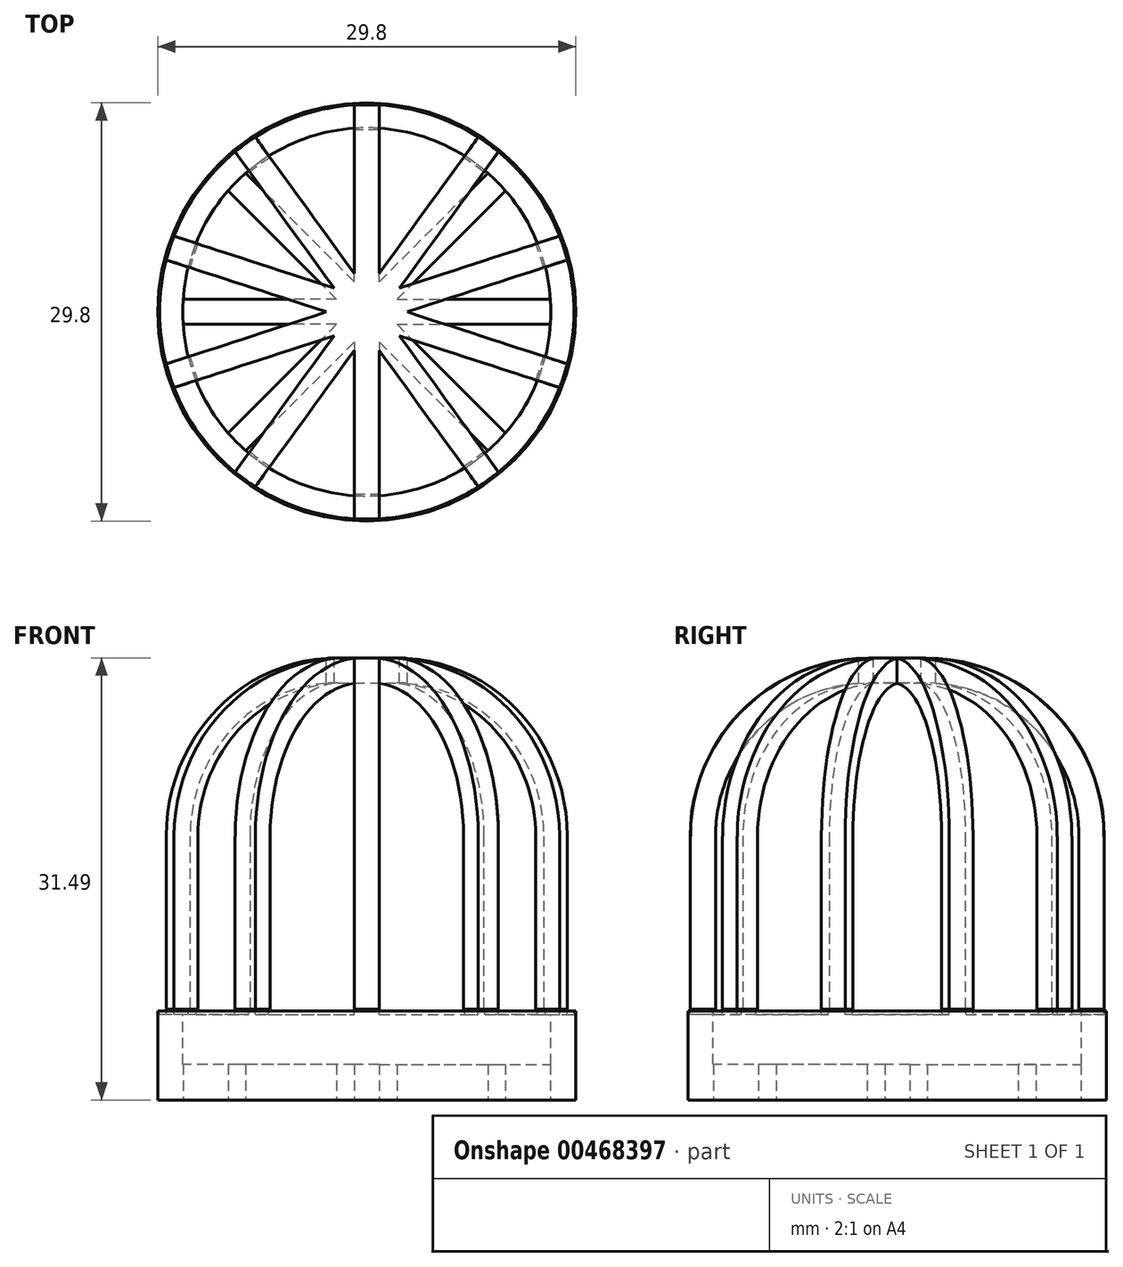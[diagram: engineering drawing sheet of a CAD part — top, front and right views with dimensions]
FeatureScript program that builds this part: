
annotation { "Feature Type Name" : "Feature", "Feature Type Description" : "" }
export const myFeature = defineFeature(function(context is Context, id is Id, definition is map)
    precondition{}
    {
        {
            var Q0;
            Q0=qCreatedBy(makeId("Top.planeOp"),FACE);
            var sketch = newSketch(context, id + "F0", { "sketchPlane" : qUnion([Q0])});
            skCircle(sketch, "E0", {"center": v(0, 0) * mm, "radius": 14.9 * mm});
            skSolve(sketch);
        }
        {
            var Q0;
            Q0 = qSketchRegion(id + "F0", true);
            extrude(context, id + "F1", {"entities" : qUnion([Q0]), "depth" : 6.35 * mm});
        }
        {
            var Q0;
            Q0=makeQuery(id+"F1.opExtrude","CAP_FACE",FACE,{"disambiguationData":[OSD([sQuery(id+"F0.wireOp",EDGE,"E0")])],"isStart":false});
            var sketch = newSketch(context, id + "F2", { "sketchPlane" : qUnion([Q0])});
            skCircle(sketch, "E1", {"center": v(0, 0) * mm, "radius": 13.12 * mm});
            skSolve(sketch);
        }
        {
            var Q0;
            Q0=makeQuery(id+"F2.imprint","IMPRINT",FACE,{"disambiguationData":[TD([[makeQuery(id+"F2.imprint","IMPRINT",EDGE,{"derivedFrom":sQuery(id+"F2.wireOp",EDGE,"E1")}),1.0]])]});
            extrude(context, id + "F3", {"entities" : qUnion([Q0]), "operationType" : NewBodyOperationType.REMOVE, "oppositeDirection" : true, "depth" : 25.4 * mm});
        }
        {
            var Q0;
            Q0=qCreatedBy(makeId("Front.planeOp"),FACE);
            var sketch = newSketch(context, id + "F4", { "sketchPlane" : qUnion([Q0])});
            skLineSegment(sketch, "E2", {"start": v(0, 6.47) * mm, "end": v(0, 31.49) * mm});
            skLineSegment(sketch, "E3", {"start": v(0, 31.49) * mm, "end": v(2.06, 31.49) * mm});
            skLineSegment(sketch, "E4", {"start": v(0, 6.47) * mm, "end": v(14.76, 6.47) * mm});
            skLineSegment(sketch, "E5", {"start": v(14.76, 6.47) * mm, "end": v(14.76, 18.79) * mm});
            skPoint(sketch, "E6.orphan", {"position": v(15.8, 31.49) * mm});
            skPoint(sketch, "E7.visualSharp", {"position": v(14.76, 31.49) * mm});
            skArc(sketch, "E7.filletArc", {"start": v(14.76, 18.79) * mm, "mid": v(11.04, 27.77) * mm, "end": v(2.06, 31.49) * mm});
            skSolve(sketch);
        }
        {
            var Q0;
            Q0 = qSketchRegion(id + "F4", true);
            var Q1;
            Q1=sQuery(id+"F4.wireOp",EDGE,"E2");
            revolve(context, id + "F5", {"operationType" : NewBodyOperationType.ADD, "entities" : qUnion([Q0]), "axis" : qUnion([Q1]), "revolveType" : RevolveType.FULL});
        }
        {
            var Q0;
            Q0=makeQuery(id+"F5.opRevolve","SWEPT_FACE",FACE,{"disambiguationData":[OSD([sQuery(id+"F4.wireOp",EDGE,"E4")])]});
            shell(context, id + "F6", {"entities" : qUnion([Q0]), "thickness" : 1.78 * mm});
        }
        {
            var Q0;
            Q0=makeQuery(id+"F5.opRevolve","SWEPT_FACE",FACE,{"disambiguationData":[OSD([sQuery(id+"F4.wireOp",EDGE,"E3")])]});
            var sketch = newSketch(context, id + "F7", { "sketchPlane" : qUnion([Q0])});
            skLineSegment(sketch, "E8", {"start": v(0, 0) * mm, "end": v(0, 14.8) * mm});
            skLineSegment(sketch, "E9", {"start": v(-0.89, 1.86) * mm, "end": v(-0.89, 14.74) * mm});
            skLineSegment(sketch, "E10", {"start": v(0.89, 1.86) * mm, "end": v(0.89, 14.74) * mm});
            skCircle(sketch, "E11", {"center": v(0, 0) * mm, "radius": 14.76 * mm});
            skLineSegment(sketch, "E12.1.0", {"start": v(-0.37, 2.02) * mm, "end": v(-7.94, 12.45) * mm});
            skLineSegment(sketch, "E12.1.1", {"start": v(-1.81, 0.98) * mm, "end": v(-9.38, 11.4) * mm});
            skLineSegment(sketch, "E12.2.0", {"start": v(-1.5, 1.42) * mm, "end": v(-13.74, 5.4) * mm});
            skLineSegment(sketch, "E12.2.1", {"start": v(-2.04, -0.27) * mm, "end": v(-14.3, 3.7) * mm});
            skLineSegment(sketch, "E12.3.0", {"start": v(-2.04, 0.27) * mm, "end": v(-14.3, -3.7) * mm});
            skLineSegment(sketch, "E12.3.1", {"start": v(-1.5, -1.42) * mm, "end": v(-13.74, -5.4) * mm});
            skLineSegment(sketch, "E12.4.0", {"start": v(-1.81, -0.98) * mm, "end": v(-9.38, -11.4) * mm});
            skLineSegment(sketch, "E12.4.1", {"start": v(-0.37, -2.02) * mm, "end": v(-7.94, -12.45) * mm});
            skLineSegment(sketch, "E12.5.0", {"start": v(-0.89, -1.86) * mm, "end": v(-0.89, -14.74) * mm});
            skLineSegment(sketch, "E12.5.1", {"start": v(0.89, -1.86) * mm, "end": v(0.89, -14.74) * mm});
            skLineSegment(sketch, "E12.6.0", {"start": v(0.37, -2.02) * mm, "end": v(7.94, -12.45) * mm});
            skLineSegment(sketch, "E12.6.1", {"start": v(1.81, -0.98) * mm, "end": v(9.38, -11.4) * mm});
            skLineSegment(sketch, "E12.7.0", {"start": v(1.5, -1.42) * mm, "end": v(13.74, -5.4) * mm});
            skLineSegment(sketch, "E12.7.1", {"start": v(2.04, 0.27) * mm, "end": v(14.3, -3.7) * mm});
            skLineSegment(sketch, "E12.8.0", {"start": v(2.04, -0.27) * mm, "end": v(14.3, 3.7) * mm});
            skLineSegment(sketch, "E12.8.1", {"start": v(1.5, 1.42) * mm, "end": v(13.74, 5.4) * mm});
            skLineSegment(sketch, "E12.9.0", {"start": v(1.81, 0.98) * mm, "end": v(9.38, 11.4) * mm});
            skLineSegment(sketch, "E12.9.1", {"start": v(0.37, 2.02) * mm, "end": v(7.94, 12.45) * mm});
            skSolve(sketch);
        }
        {
            var Q0;
            {var subQ0=sQuery(id+"F7.wireOp",EDGE,"E12.4.1");var subQ1=sQuery(id+"F7.wireOp",EDGE,"E11");var subQ2=makeQuery(id+"F7.imprint","INTERSECT",VERTEX,{"derivedFrom":[subQ1,subQ0]});Q0=makeQuery(id+"F7.imprint","IMPRINT",FACE,{"disambiguationData":[TD([[makeQuery(id+"F7.imprint","IMPRINT",EDGE,{"disambiguationData":[TD([[subQ2,-1.0]])],"derivedFrom":subQ1}),1.0]])]});}
            var Q1;
            {var subQ0=sQuery(id+"F7.wireOp",EDGE,"E12.3.1");var subQ1=sQuery(id+"F7.wireOp",EDGE,"E11");var subQ2=makeQuery(id+"F7.imprint","INTERSECT",VERTEX,{"derivedFrom":[subQ1,subQ0]});Q1=makeQuery(id+"F7.imprint","IMPRINT",FACE,{"disambiguationData":[TD([[makeQuery(id+"F7.imprint","IMPRINT",EDGE,{"disambiguationData":[TD([[subQ2,-1.0]])],"derivedFrom":subQ1}),1.0]])]});}
            var Q2;
            {var subQ0=sQuery(id+"F7.wireOp",EDGE,"E12.2.1");var subQ1=sQuery(id+"F7.wireOp",EDGE,"E11");var subQ2=makeQuery(id+"F7.imprint","INTERSECT",VERTEX,{"derivedFrom":[subQ1,subQ0]});Q2=makeQuery(id+"F7.imprint","IMPRINT",FACE,{"disambiguationData":[TD([[makeQuery(id+"F7.imprint","IMPRINT",EDGE,{"disambiguationData":[TD([[subQ2,-1.0]])],"derivedFrom":subQ1}),1.0]])]});}
            var Q3;
            {var subQ0=sQuery(id+"F7.wireOp",EDGE,"E12.5.1");var subQ1=sQuery(id+"F7.wireOp",EDGE,"E11");var subQ2=makeQuery(id+"F7.imprint","INTERSECT",VERTEX,{"derivedFrom":[subQ1,subQ0]});Q3=makeQuery(id+"F7.imprint","IMPRINT",FACE,{"disambiguationData":[TD([[makeQuery(id+"F7.imprint","IMPRINT",EDGE,{"disambiguationData":[TD([[subQ2,-1.0]])],"derivedFrom":subQ1}),1.0]])]});}
            var Q4;
            {var subQ0=sQuery(id+"F7.wireOp",EDGE,"E12.6.1");var subQ1=sQuery(id+"F7.wireOp",EDGE,"E11");var subQ2=makeQuery(id+"F7.imprint","INTERSECT",VERTEX,{"derivedFrom":[subQ1,subQ0]});Q4=makeQuery(id+"F7.imprint","IMPRINT",FACE,{"disambiguationData":[TD([[makeQuery(id+"F7.imprint","IMPRINT",EDGE,{"disambiguationData":[TD([[subQ2,-1.0]])],"derivedFrom":subQ1}),1.0]])]});}
            var Q5;
            {var subQ0=sQuery(id+"F7.wireOp",EDGE,"E12.7.1");var subQ1=sQuery(id+"F7.wireOp",EDGE,"E11");var subQ2=makeQuery(id+"F7.imprint","INTERSECT",VERTEX,{"derivedFrom":[subQ1,subQ0]});Q5=makeQuery(id+"F7.imprint","IMPRINT",FACE,{"disambiguationData":[TD([[makeQuery(id+"F7.imprint","IMPRINT",EDGE,{"disambiguationData":[TD([[subQ2,-1.0]])],"derivedFrom":subQ1}),1.0]])]});}
            var Q6;
            {var subQ0=sQuery(id+"F7.wireOp",EDGE,"E12.8.1");var subQ1=sQuery(id+"F7.wireOp",EDGE,"E11");var subQ2=makeQuery(id+"F7.imprint","INTERSECT",VERTEX,{"derivedFrom":[subQ1,subQ0]});Q6=makeQuery(id+"F7.imprint","IMPRINT",FACE,{"disambiguationData":[TD([[makeQuery(id+"F7.imprint","IMPRINT",EDGE,{"disambiguationData":[TD([[subQ2,-1.0]])],"derivedFrom":subQ1}),1.0]])]});}
            var Q7;
            {var subQ0=sQuery(id+"F7.wireOp",EDGE,"E11");var subQ1=sQuery(id+"F7.wireOp",EDGE,"E10");var subQ2=makeQuery(id+"F7.imprint","INTERSECT",VERTEX,{"derivedFrom":[subQ1,subQ0]});Q7=makeQuery(id+"F7.imprint","IMPRINT",FACE,{"disambiguationData":[TD([[makeQuery(id+"F7.imprint","IMPRINT",EDGE,{"disambiguationData":[TD([[subQ2,1.0]])],"derivedFrom":subQ1}),-1.0]])]});}
            var Q8;
            {var subQ0=sQuery(id+"F7.wireOp",EDGE,"E11");var subQ1=sQuery(id+"F7.wireOp",EDGE,"E9");var subQ2=makeQuery(id+"F7.imprint","INTERSECT",VERTEX,{"derivedFrom":[subQ1,subQ0]});Q8=makeQuery(id+"F7.imprint","IMPRINT",FACE,{"disambiguationData":[TD([[makeQuery(id+"F7.imprint","IMPRINT",EDGE,{"disambiguationData":[TD([[subQ2,1.0]])],"derivedFrom":subQ1}),1.0]])]});}
            var Q9;
            {var subQ0=sQuery(id+"F7.wireOp",EDGE,"E12.1.1");var subQ1=sQuery(id+"F7.wireOp",EDGE,"E11");var subQ2=makeQuery(id+"F7.imprint","INTERSECT",VERTEX,{"derivedFrom":[subQ1,subQ0]});Q9=makeQuery(id+"F7.imprint","IMPRINT",FACE,{"disambiguationData":[TD([[makeQuery(id+"F7.imprint","IMPRINT",EDGE,{"disambiguationData":[TD([[subQ2,-1.0]])],"derivedFrom":subQ1}),1.0]])]});}
            extrude(context, id + "F8", {"entities" : qUnion([Q0, Q1, Q2, Q3, Q4, Q5, Q6, Q7, Q8, Q9]), "operationType" : NewBodyOperationType.REMOVE, "oppositeDirection" : true, "depth" : 25.4 * mm});
        }
        {
            var Q0;
            Q0=makeQuery(id+"F1.opExtrude","CAP_FACE",FACE,{"disambiguationData":[OSD([sQuery(id+"F0.wireOp",EDGE,"E0")])],"isStart":true});
            var sketch = newSketch(context, id + "F9", { "sketchPlane" : qUnion([Q0])});
            skCircle(sketch, "E13", {"center": v(0, 0) * mm, "radius": 13.3 * mm});
            skLineSegment(sketch, "E14", {"start": v(0, 0) * mm, "end": v(0, 13.3) * mm});
            skLineSegment(sketch, "E15", {"start": v(0.89, 0) * mm, "end": v(0.89, 13.27) * mm});
            skLineSegment(sketch, "E16", {"start": v(-0.89, 0) * mm, "end": v(-0.89, 13.27) * mm});
            skLineSegment(sketch, "E17.1.0", {"start": v(-0.63, -0.63) * mm, "end": v(-10.01, 8.75) * mm});
            skLineSegment(sketch, "E17.1.1", {"start": v(0.63, 0.63) * mm, "end": v(-8.75, 10.01) * mm});
            skLineSegment(sketch, "E17.2.0", {"start": v(0, -0.89) * mm, "end": v(-13.27, -0.89) * mm});
            skLineSegment(sketch, "E17.2.1", {"start": v(0, 0.89) * mm, "end": v(-13.27, 0.89) * mm});
            skLineSegment(sketch, "E17.3.0", {"start": v(0.63, -0.63) * mm, "end": v(-8.75, -10.01) * mm});
            skLineSegment(sketch, "E17.3.1", {"start": v(-0.63, 0.63) * mm, "end": v(-10.01, -8.75) * mm});
            skLineSegment(sketch, "E17.4.0", {"start": v(0.89, 0) * mm, "end": v(0.89, -13.27) * mm});
            skLineSegment(sketch, "E17.4.1", {"start": v(-0.89, 0) * mm, "end": v(-0.89, -13.27) * mm});
            skLineSegment(sketch, "E17.5.0", {"start": v(0.63, 0.63) * mm, "end": v(10.01, -8.75) * mm});
            skLineSegment(sketch, "E17.5.1", {"start": v(-0.63, -0.63) * mm, "end": v(8.75, -10.01) * mm});
            skLineSegment(sketch, "E17.6.0", {"start": v(0, 0.89) * mm, "end": v(13.27, 0.89) * mm});
            skLineSegment(sketch, "E17.6.1", {"start": v(0, -0.89) * mm, "end": v(13.27, -0.89) * mm});
            skLineSegment(sketch, "E17.7.0", {"start": v(-0.63, 0.63) * mm, "end": v(8.75, 10.01) * mm});
            skLineSegment(sketch, "E17.7.1", {"start": v(0.63, -0.63) * mm, "end": v(10.01, 8.75) * mm});
            skSolve(sketch);
        }
        {
            var Q0;
            {var subQ0=sQuery(id+"F9.wireOp",EDGE,"E17.7.0");var subQ5=sQuery(id+"F9.wireOp",EDGE,"E15");var subQ6=makeQuery(id+"F9.imprint","INTERSECT",VERTEX,{"derivedFrom":[subQ5,subQ0]});Q0=makeQuery(id+"F9.imprint","IMPRINT",FACE,{"disambiguationData":[TD([[makeQuery(id+"F9.imprint","IMPRINT",EDGE,{"disambiguationData":[TD([[subQ6,-1.0]])],"derivedFrom":subQ5}),1.0]])]});}
            var Q1;
            {var subQ0=sQuery(id+"F9.wireOp",EDGE,"E17.1.1");var subQ5=sQuery(id+"F9.wireOp",EDGE,"E16");var subQ6=makeQuery(id+"F9.imprint","INTERSECT",VERTEX,{"derivedFrom":[subQ5,subQ0]});Q1=makeQuery(id+"F9.imprint","IMPRINT",FACE,{"disambiguationData":[TD([[makeQuery(id+"F9.imprint","IMPRINT",EDGE,{"disambiguationData":[TD([[subQ6,-1.0]])],"derivedFrom":subQ5}),-1.0]])]});}
            var Q2;
            {var subQ1=sQuery(id+"F9.wireOp",EDGE,"E17.6.0");var subQ6=sQuery(id+"F9.wireOp",EDGE,"E15");var subQ9=makeQuery(id+"F9.imprint","INTERSECT",VERTEX,{"derivedFrom":[subQ6,subQ1]});Q2=makeQuery(id+"F9.imprint","IMPRINT",FACE,{"disambiguationData":[TD([[makeQuery(id+"F9.imprint","IMPRINT",EDGE,{"disambiguationData":[TD([[subQ9,-1.0]])],"derivedFrom":subQ6}),-1.0]])]});}
            var Q3;
            {var subQ1=sQuery(id+"F9.wireOp",EDGE,"E17.1.0");var subQ5=sQuery(id+"F9.wireOp",EDGE,"E17.3.1");var subQ9=makeQuery(id+"F9.imprint","INTERSECT",VERTEX,{"derivedFrom":[subQ1,subQ5]});Q3=makeQuery(id+"F9.imprint","IMPRINT",FACE,{"disambiguationData":[TD([[makeQuery(id+"F9.imprint","IMPRINT",EDGE,{"disambiguationData":[TD([[subQ9,-1.0]])],"derivedFrom":subQ1}),1.0]])]});}
            var Q4;
            {var subQ1=sQuery(id+"F9.wireOp",EDGE,"E17.2.0");var subQ5=sQuery(id+"F9.wireOp",EDGE,"E17.4.1");var subQ9=makeQuery(id+"F9.imprint","INTERSECT",VERTEX,{"derivedFrom":[subQ1,subQ5]});Q4=makeQuery(id+"F9.imprint","IMPRINT",FACE,{"disambiguationData":[TD([[makeQuery(id+"F9.imprint","IMPRINT",EDGE,{"disambiguationData":[TD([[subQ9,-1.0]])],"derivedFrom":subQ1}),1.0]])]});}
            var Q5;
            {var subQ1=sQuery(id+"F9.wireOp",EDGE,"E16");var subQ5=sQuery(id+"F9.wireOp",EDGE,"E17.2.1");var subQ6=makeQuery(id+"F9.imprint","INTERSECT",VERTEX,{"derivedFrom":[subQ1,subQ5]});Q5=makeQuery(id+"F9.imprint","IMPRINT",FACE,{"disambiguationData":[TD([[makeQuery(id+"F9.imprint","IMPRINT",EDGE,{"disambiguationData":[TD([[subQ6,-1.0]])],"derivedFrom":subQ1}),1.0]])]});}
            var Q6;
            {var subQ1=sQuery(id+"F9.wireOp",EDGE,"E17.5.0");var subQ5=sQuery(id+"F9.wireOp",EDGE,"E17.7.1");var subQ9=makeQuery(id+"F9.imprint","INTERSECT",VERTEX,{"derivedFrom":[subQ1,subQ5]});Q6=makeQuery(id+"F9.imprint","IMPRINT",FACE,{"disambiguationData":[TD([[makeQuery(id+"F9.imprint","IMPRINT",EDGE,{"disambiguationData":[TD([[subQ9,-1.0]])],"derivedFrom":subQ1}),1.0]])]});}
            var Q7;
            {var subQ1=sQuery(id+"F9.wireOp",EDGE,"E17.4.0");var subQ5=sQuery(id+"F9.wireOp",EDGE,"E17.6.1");var subQ9=makeQuery(id+"F9.imprint","INTERSECT",VERTEX,{"derivedFrom":[subQ1,subQ5]});Q7=makeQuery(id+"F9.imprint","IMPRINT",FACE,{"disambiguationData":[TD([[makeQuery(id+"F9.imprint","IMPRINT",EDGE,{"disambiguationData":[TD([[subQ9,-1.0]])],"derivedFrom":subQ1}),1.0]])]});}
            var Q8;
            {var subQ1=sQuery(id+"F9.wireOp",EDGE,"E17.3.0");var subQ5=sQuery(id+"F9.wireOp",EDGE,"E17.5.1");var subQ9=makeQuery(id+"F9.imprint","INTERSECT",VERTEX,{"derivedFrom":[subQ1,subQ5]});Q8=makeQuery(id+"F9.imprint","IMPRINT",FACE,{"disambiguationData":[TD([[makeQuery(id+"F9.imprint","IMPRINT",EDGE,{"disambiguationData":[TD([[subQ9,-1.0]])],"derivedFrom":subQ1}),1.0]])]});}
            var Q9;
            {var subQ5=sQuery(id+"F9.wireOp",EDGE,"E17.4.0");var subQ6=sQuery(id+"F9.wireOp",EDGE,"E15");var subQ7=makeQuery(id+"F9.imprint","INTERSECT",VERTEX,{"derivedFrom":[subQ6,subQ5]});Q9=makeQuery(id+"F9.imprint","IMPRINT",FACE,{"disambiguationData":[TD([[makeQuery(id+"F9.imprint","IMPRINT",EDGE,{"disambiguationData":[TD([[subQ7,-1.0]])],"derivedFrom":subQ6}),1.0]])]});}
            var Q10;
            {var subQ0=sQuery(id+"F9.wireOp",EDGE,"E17.3.1");var subQ1=sQuery(id+"F9.wireOp",EDGE,"E16");var subQ2=makeQuery(id+"F9.imprint","INTERSECT",VERTEX,{"derivedFrom":[subQ1,subQ0]});Q10=makeQuery(id+"F9.imprint","IMPRINT",FACE,{"disambiguationData":[TD([[makeQuery(id+"F9.imprint","IMPRINT",EDGE,{"disambiguationData":[TD([[subQ2,-1.0]])],"derivedFrom":subQ1}),-1.0]])]});}
            var Q11;
            {var subQ0=sQuery(id+"F9.wireOp",EDGE,"E17.5.0");var subQ1=sQuery(id+"F9.wireOp",EDGE,"E15");var subQ2=makeQuery(id+"F9.imprint","INTERSECT",VERTEX,{"derivedFrom":[subQ1,subQ0]});Q11=makeQuery(id+"F9.imprint","IMPRINT",FACE,{"disambiguationData":[TD([[makeQuery(id+"F9.imprint","IMPRINT",EDGE,{"disambiguationData":[TD([[subQ2,-1.0]])],"derivedFrom":subQ1}),1.0]])]});}
            var Q12;
            {var subQ0=sQuery(id+"F9.wireOp",EDGE,"E17.4.0");var subQ1=sQuery(id+"F9.wireOp",EDGE,"E15");var subQ2=makeQuery(id+"F9.imprint","INTERSECT",VERTEX,{"derivedFrom":[subQ1,subQ0]});Q12=makeQuery(id+"F9.imprint","IMPRINT",FACE,{"disambiguationData":[TD([[makeQuery(id+"F9.imprint","IMPRINT",EDGE,{"disambiguationData":[TD([[subQ2,-1.0]])],"derivedFrom":subQ1}),-1.0]])]});}
            var Q13;
            {var subQ0=sQuery(id+"F9.wireOp",EDGE,"E17.6.1");var subQ1=sQuery(id+"F9.wireOp",EDGE,"E17.2.0");var subQ2=makeQuery(id+"F9.imprint","INTERSECT",VERTEX,{"derivedFrom":[subQ1,subQ0]});Q13=makeQuery(id+"F9.imprint","IMPRINT",FACE,{"disambiguationData":[TD([[makeQuery(id+"F9.imprint","IMPRINT",EDGE,{"disambiguationData":[TD([[subQ2,-1.0]])],"derivedFrom":subQ1}),1.0]])]});}
            var Q14;
            {var subQ0=sQuery(id+"F9.wireOp",EDGE,"E17.7.1");var subQ1=sQuery(id+"F9.wireOp",EDGE,"E17.3.0");var subQ2=makeQuery(id+"F9.imprint","INTERSECT",VERTEX,{"derivedFrom":[subQ1,subQ0]});Q14=makeQuery(id+"F9.imprint","IMPRINT",FACE,{"disambiguationData":[TD([[makeQuery(id+"F9.imprint","IMPRINT",EDGE,{"disambiguationData":[TD([[subQ2,-1.0]])],"derivedFrom":subQ1}),1.0]])]});}
            var Q15;
            {var subQ0=sQuery(id+"F9.wireOp",EDGE,"E17.5.1");var subQ1=sQuery(id+"F9.wireOp",EDGE,"E17.1.0");var subQ2=makeQuery(id+"F9.imprint","INTERSECT",VERTEX,{"derivedFrom":[subQ1,subQ0]});Q15=makeQuery(id+"F9.imprint","IMPRINT",FACE,{"disambiguationData":[TD([[makeQuery(id+"F9.imprint","IMPRINT",EDGE,{"disambiguationData":[TD([[subQ2,-1.0]])],"derivedFrom":subQ1}),1.0]])]});}
            var Q16;
            {var subQ0=sQuery(id+"F9.wireOp",EDGE,"E17.4.1");var subQ1=sQuery(id+"F9.wireOp",EDGE,"E16");var subQ2=makeQuery(id+"F9.imprint","INTERSECT",VERTEX,{"derivedFrom":[subQ1,subQ0]});Q16=makeQuery(id+"F9.imprint","IMPRINT",FACE,{"disambiguationData":[TD([[makeQuery(id+"F9.imprint","IMPRINT",EDGE,{"disambiguationData":[TD([[subQ2,-1.0]])],"derivedFrom":subQ1}),1.0]])]});}
            var Q17;
            {var subQ0=sQuery(id+"F9.wireOp",EDGE,"E17.3.1");var subQ1=sQuery(id+"F9.wireOp",EDGE,"E16");var subQ2=makeQuery(id+"F9.imprint","INTERSECT",VERTEX,{"derivedFrom":[subQ1,subQ0]});Q17=makeQuery(id+"F9.imprint","IMPRINT",FACE,{"disambiguationData":[TD([[makeQuery(id+"F9.imprint","IMPRINT",EDGE,{"disambiguationData":[TD([[subQ2,-1.0]])],"derivedFrom":subQ1}),1.0]])]});}
            var Q18;
            {var subQ0=sQuery(id+"F9.wireOp",EDGE,"E17.2.1");var subQ1=sQuery(id+"F9.wireOp",EDGE,"E16");var subQ2=makeQuery(id+"F9.imprint","INTERSECT",VERTEX,{"derivedFrom":[subQ1,subQ0]});Q18=makeQuery(id+"F9.imprint","IMPRINT",FACE,{"disambiguationData":[TD([[makeQuery(id+"F9.imprint","IMPRINT",EDGE,{"disambiguationData":[TD([[subQ2,-1.0]])],"derivedFrom":subQ1}),-1.0]])]});}
            var Q19;
            {var subQ0=sQuery(id+"F9.wireOp",EDGE,"E17.6.0");var subQ3=sQuery(id+"F9.wireOp",EDGE,"E17.1.1");var subQ5=makeQuery(id+"F9.imprint","INTERSECT",VERTEX,{"derivedFrom":[subQ3,subQ0]});Q19=makeQuery(id+"F9.imprint","IMPRINT",FACE,{"disambiguationData":[TD([[makeQuery(id+"F9.imprint","IMPRINT",EDGE,{"disambiguationData":[TD([[subQ5,-1.0]])],"derivedFrom":subQ3}),1.0]])]});}
            var Q20;
            {var subQ0=sQuery(id+"F9.wireOp",EDGE,"E17.2.1");var subQ3=sQuery(id+"F9.wireOp",EDGE,"E17.7.0");var subQ5=makeQuery(id+"F9.imprint","INTERSECT",VERTEX,{"derivedFrom":[subQ0,subQ3]});Q20=makeQuery(id+"F9.imprint","IMPRINT",FACE,{"disambiguationData":[TD([[makeQuery(id+"F9.imprint","IMPRINT",EDGE,{"disambiguationData":[TD([[subQ5,1.0]])],"derivedFrom":subQ0}),-1.0]])]});}
            var Q21;
            {var subQ0=sQuery(id+"F9.wireOp",EDGE,"E17.6.0");var subQ1=sQuery(id+"F9.wireOp",EDGE,"E15");var subQ2=makeQuery(id+"F9.imprint","INTERSECT",VERTEX,{"derivedFrom":[subQ1,subQ0]});Q21=makeQuery(id+"F9.imprint","IMPRINT",FACE,{"disambiguationData":[TD([[makeQuery(id+"F9.imprint","IMPRINT",EDGE,{"disambiguationData":[TD([[subQ2,-1.0]])],"derivedFrom":subQ1}),1.0]])]});}
            var Q22;
            {var subQ0=sQuery(id+"F9.wireOp",EDGE,"E17.5.0");var subQ1=sQuery(id+"F9.wireOp",EDGE,"E15");var subQ2=makeQuery(id+"F9.imprint","INTERSECT",VERTEX,{"derivedFrom":[subQ1,subQ0]});Q22=makeQuery(id+"F9.imprint","IMPRINT",FACE,{"disambiguationData":[TD([[makeQuery(id+"F9.imprint","IMPRINT",EDGE,{"disambiguationData":[TD([[subQ2,-1.0]])],"derivedFrom":subQ1}),-1.0]])]});}
            var Q23;
            {var subQ0=sQuery(id+"F9.wireOp",EDGE,"E17.7.1");var subQ1=sQuery(id+"F9.wireOp",EDGE,"E17.4.0");var subQ2=makeQuery(id+"F9.imprint","INTERSECT",VERTEX,{"derivedFrom":[subQ1,subQ0]});Q23=makeQuery(id+"F9.imprint","IMPRINT",FACE,{"disambiguationData":[TD([[makeQuery(id+"F9.imprint","IMPRINT",EDGE,{"disambiguationData":[TD([[subQ2,-1.0]])],"derivedFrom":subQ1}),1.0]])]});}
            var Q24;
            {var subQ0=sQuery(id+"F9.wireOp",EDGE,"E17.6.1");var subQ1=sQuery(id+"F9.wireOp",EDGE,"E17.3.0");var subQ2=makeQuery(id+"F9.imprint","INTERSECT",VERTEX,{"derivedFrom":[subQ1,subQ0]});Q24=makeQuery(id+"F9.imprint","IMPRINT",FACE,{"disambiguationData":[TD([[makeQuery(id+"F9.imprint","IMPRINT",EDGE,{"disambiguationData":[TD([[subQ2,-1.0]])],"derivedFrom":subQ1}),1.0]])]});}
            var Q25;
            {var subQ0=sQuery(id+"F9.wireOp",EDGE,"E17.5.1");var subQ1=sQuery(id+"F9.wireOp",EDGE,"E17.2.0");var subQ2=makeQuery(id+"F9.imprint","INTERSECT",VERTEX,{"derivedFrom":[subQ1,subQ0]});Q25=makeQuery(id+"F9.imprint","IMPRINT",FACE,{"disambiguationData":[TD([[makeQuery(id+"F9.imprint","IMPRINT",EDGE,{"disambiguationData":[TD([[subQ2,-1.0]])],"derivedFrom":subQ1}),1.0]])]});}
            var Q26;
            {var subQ0=sQuery(id+"F9.wireOp",EDGE,"E17.4.1");var subQ1=sQuery(id+"F9.wireOp",EDGE,"E17.1.0");var subQ2=makeQuery(id+"F9.imprint","INTERSECT",VERTEX,{"derivedFrom":[subQ1,subQ0]});Q26=makeQuery(id+"F9.imprint","IMPRINT",FACE,{"disambiguationData":[TD([[makeQuery(id+"F9.imprint","IMPRINT",EDGE,{"disambiguationData":[TD([[subQ2,-1.0]])],"derivedFrom":subQ1}),1.0]])]});}
            extrude(context, id + "F10", {"entities" : qUnion([Q0, Q1, Q2, Q3, Q4, Q5, Q6, Q7, Q8, Q9, Q10, Q11, Q12, Q13, Q14, Q15, Q16, Q17, Q18, Q19, Q20, Q21, Q22, Q23, Q24, Q25, Q26]), "operationType" : NewBodyOperationType.ADD, "oppositeDirection" : true, "depth" : 2.54 * mm});
        }
    });
